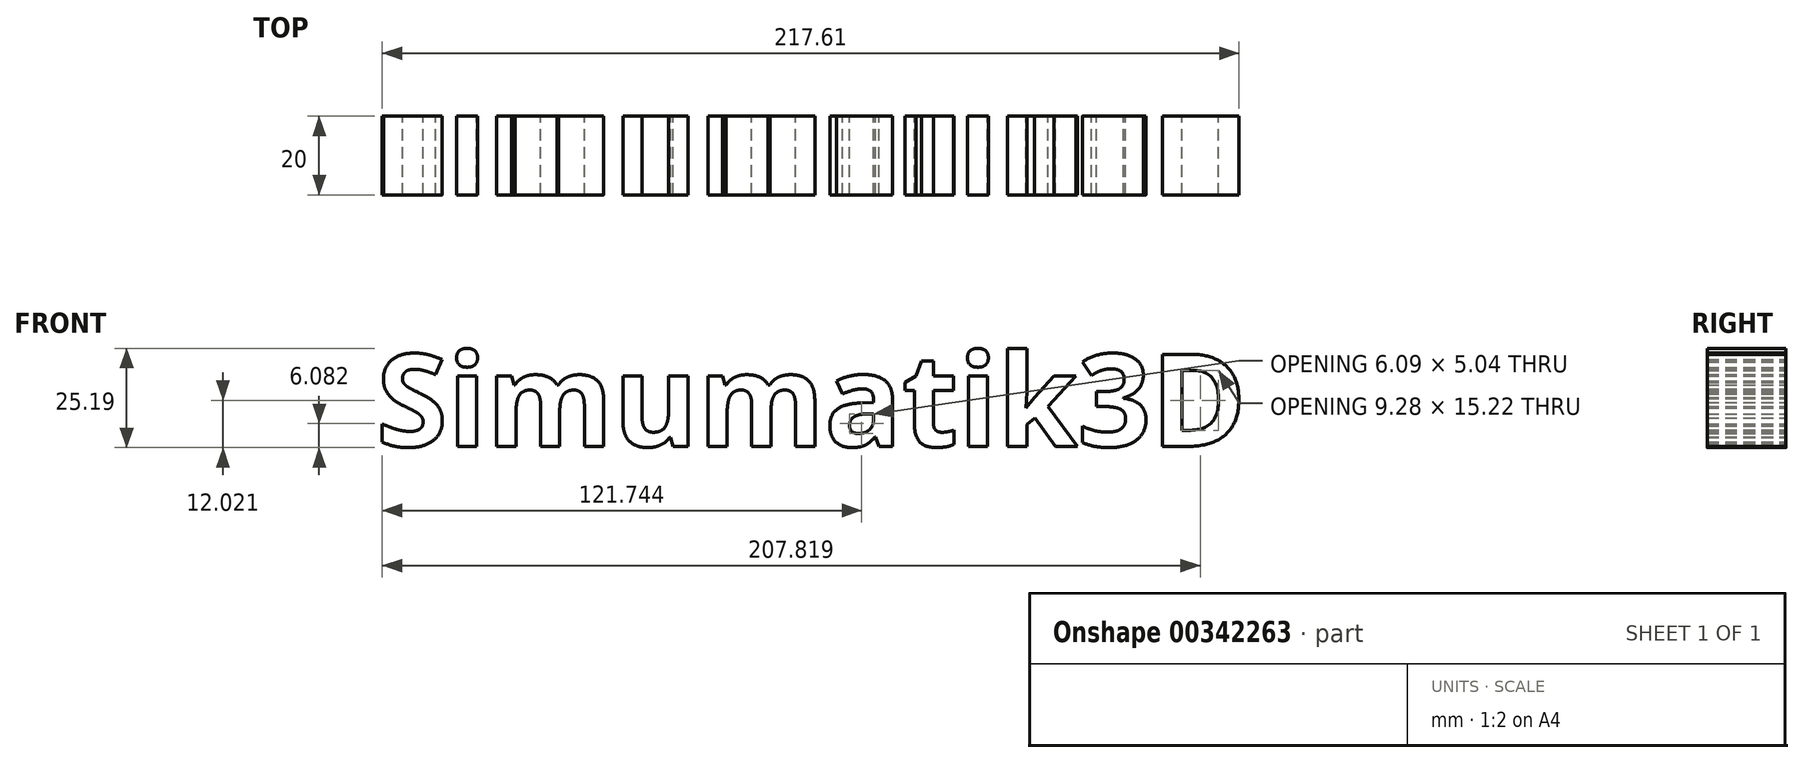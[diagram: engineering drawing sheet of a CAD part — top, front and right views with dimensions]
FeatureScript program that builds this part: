
annotation { "Feature Type Name" : "Feature", "Feature Type Description" : "" }
export const myFeature = defineFeature(function(context is Context, id is Id, definition is map)
    precondition{}
    {
        {
            var Q0;
            Q0=qCreatedBy(makeId("Front.planeOp"),FACE);
            var sketch = newSketch(context, id + "F0", { "sketchPlane" : qUnion([Q0])});
            skText(sketch, "E0", { "text": "Simumatik3D", "fontName": "OpenSans-Bold.ttf"});
            const initialGuessF0  = {"E0": [-0.1029, 5e-05, 1, 0, 0.02357]};
            skSetInitialGuess(sketch, initialGuessF0);
            skSolve(sketch);
        }
        {
            var Q0;
            Q0 = qSketchRegion(id + "F0", true);
            extrude(context, id + "F1", {"entities" : qUnion([Q0]), "depth" : 20 * mm});
        }
    });
